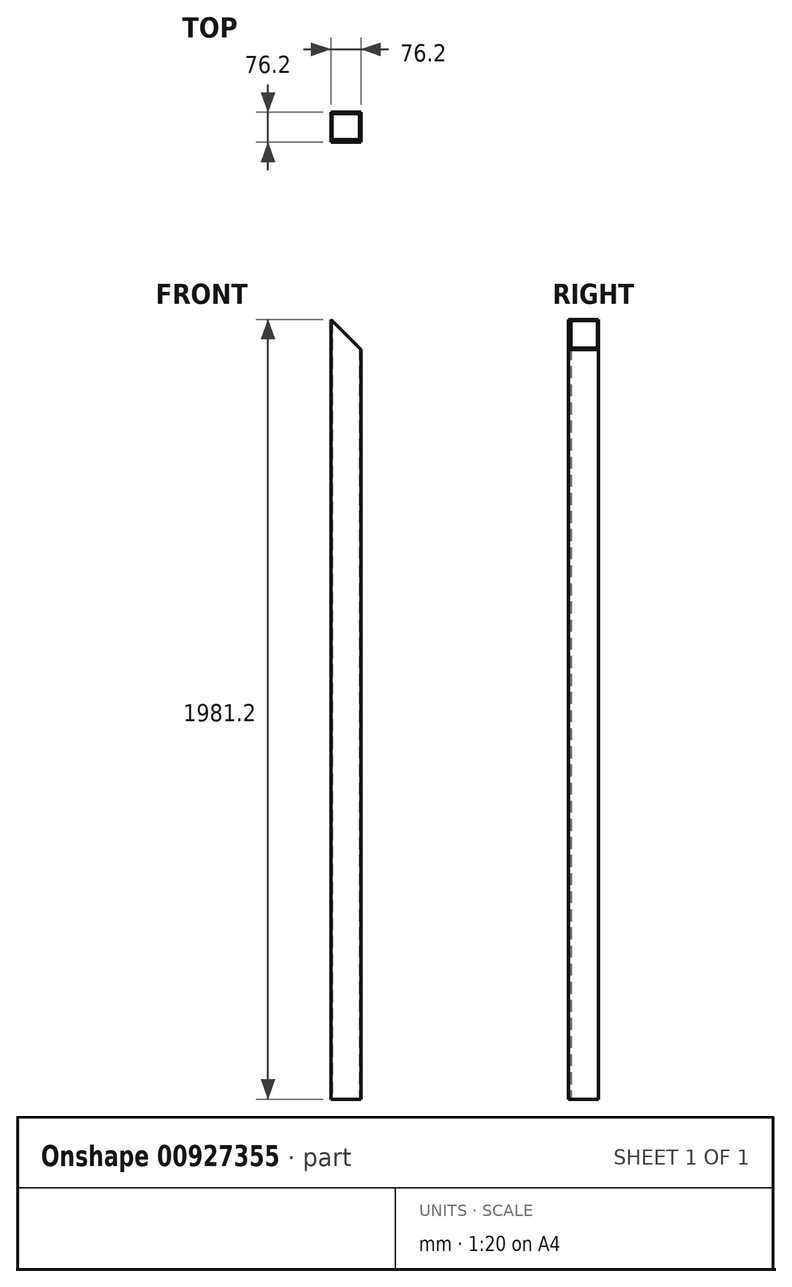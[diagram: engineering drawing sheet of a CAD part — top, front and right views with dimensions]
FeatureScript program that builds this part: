
annotation { "Feature Type Name" : "Feature", "Feature Type Description" : "" }
export const myFeature = defineFeature(function(context is Context, id is Id, definition is map)
    precondition{}
    {
        {
            var Q0;
            Q0=qCreatedBy(makeId("Top.planeOp"),FACE);
            var sketch = newSketch(context, id + "F0", { "sketchPlane" : qUnion([Q0])});
            skLineSegment(sketch, "E0.bottom", {"start": v(-38.1, 38.1) * mm, "end": v(38.1, 38.1) * mm});
            skLineSegment(sketch, "E0.top", {"start": v(-38.1, -38.1) * mm, "end": v(38.1, -38.1) * mm});
            skLineSegment(sketch, "E0.left", {"start": v(-38.1, 38.1) * mm, "end": v(-38.1, -38.1) * mm});
            skLineSegment(sketch, "E0.right", {"start": v(38.1, 38.1) * mm, "end": v(38.1, -38.1) * mm});
            skLineSegment(sketch, "E1.bottom", {"start": v(-34.93, 34.92) * mm, "end": v(34.92, 34.93) * mm});
            skLineSegment(sketch, "E1.top", {"start": v(-34.92, -31.48) * mm, "end": v(34.93, -31.48) * mm});
            skLineSegment(sketch, "E1.left", {"start": v(-34.93, 34.92) * mm, "end": v(-34.92, -31.48) * mm});
            skLineSegment(sketch, "E1.right", {"start": v(34.92, 34.93) * mm, "end": v(34.93, -31.48) * mm});
            skSolve(sketch);
        }
        {
            var Q0;
            Q0=makeQuery(id+"F0.imprint","IMPRINT",FACE,{"disambiguationData":[TD([[makeQuery(id+"F0.imprint","IMPRINT",EDGE,{"derivedFrom":sQuery(id+"F0.wireOp",EDGE,"E0.bottom")}),-1.0]])]});
            extrude(context, id + "F1", {"entities" : qUnion([Q0]), "depth" : 1981.2 * mm, "offsetDistance" : 25.4 * mm});
        }
        {
            var Q0;
            Q0=makeQuery(id+"F1.opExtrude","SWEPT_FACE",FACE,{"disambiguationData":[OSD([sQuery(id+"F0.wireOp",EDGE,"E0.top")])]});
            var sketch = newSketch(context, id + "F2", { "sketchPlane" : qUnion([Q0])});
            skLineSegment(sketch, "E2", {"start": v(-38.1, 1981.2) * mm, "end": v(76.74, 1866.36) * mm});
            skSolve(sketch);
        }
        {
            var Q0;
            {var subQ1=sQuery(id+"F0.wireOp",EDGE,"E0.top");var subQ2=makeQuery(id+"F1.opExtrude","CAP_EDGE",EDGE,{"disambiguationData":[OSD([subQ1])],"isStart":false});Q0=makeQuery(id+"F2.imprint","IMPRINT",FACE,{"disambiguationData":[TD([[makeQuery(id+"F2.imprint","IMPRINT",EDGE,{"derivedFrom":subQ2}),-1.0]])]});}
            extrude(context, id + "F3", {"entities" : qUnion([Q0]), "operationType" : NewBodyOperationType.REMOVE, "oppositeDirection" : true, "depth" : 101.6 * mm, "offsetDistance" : 25.4 * mm});
        }
    });
